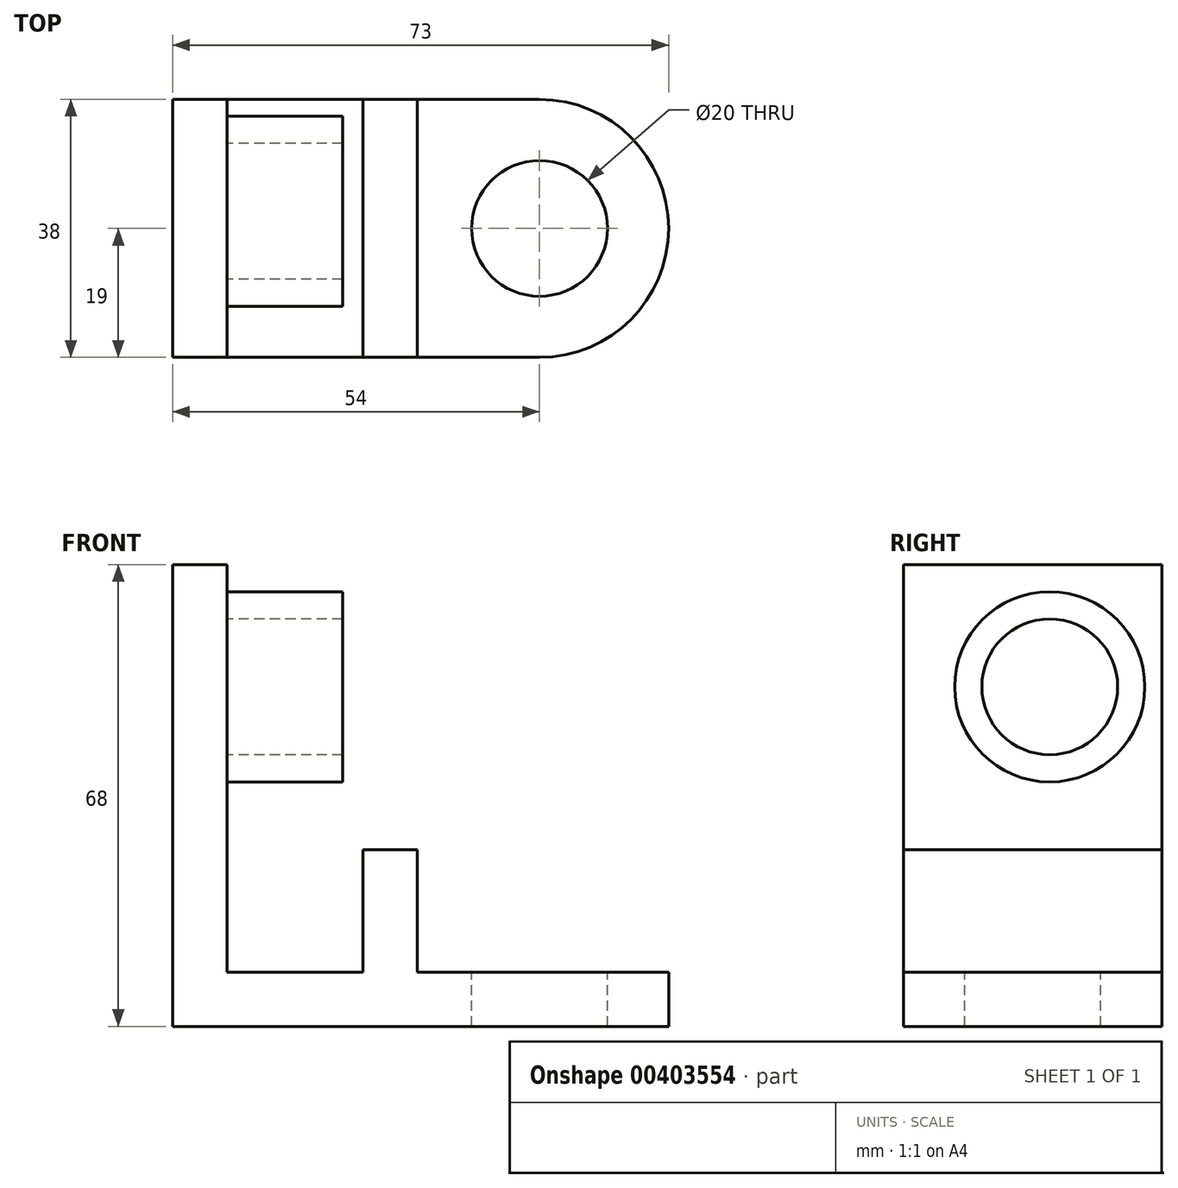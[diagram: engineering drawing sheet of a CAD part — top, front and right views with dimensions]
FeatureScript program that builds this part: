
annotation { "Feature Type Name" : "Feature", "Feature Type Description" : "" }
export const myFeature = defineFeature(function(context is Context, id is Id, definition is map)
    precondition{}
    {
        {
            var Q0;
            Q0=qCreatedBy(makeId("Front.planeOp"),FACE);
            var sketch = newSketch(context, id + "F0", { "sketchPlane" : qUnion([Q0])});
            skLineSegment(sketch, "E0", {"start": v(0, 0) * mm, "end": v(0, 68) * mm});
            skLineSegment(sketch, "E1", {"start": v(0, 68) * mm, "end": v(8, 68) * mm});
            skLineSegment(sketch, "E2", {"start": v(8, 68) * mm, "end": v(8, 8) * mm});
            skLineSegment(sketch, "E3", {"start": v(8, 8) * mm, "end": v(73, 8) * mm});
            skLineSegment(sketch, "E4", {"start": v(73, 8) * mm, "end": v(73, 0) * mm});
            skLineSegment(sketch, "E5", {"start": v(73, 0) * mm, "end": v(0, 0) * mm});
            skSolve(sketch);
        }
        {
            var Q0;
            Q0 = qSketchRegion(id + "F0", true);
            extrude(context, id + "F1", {"entities" : qUnion([Q0]), "endBound" : BoundingType.SYMMETRIC, "depth" : 38 * mm});
        }
        {
            var Q0;
            Q0=makeQuery(id+"F1.opExtrude","SWEPT_FACE",FACE,{"disambiguationData":[OSD([sQuery(id+"F0.wireOp",EDGE,"E2")])]});
            var sketch = newSketch(context, id + "F2", { "sketchPlane" : qUnion([Q0])});
            skCircle(sketch, "E6", {"center": v(2.52, 50) * mm, "radius": 14 * mm});
            skCircle(sketch, "E7", {"center": v(2.52, 50) * mm, "radius": 10 * mm});
            skSolve(sketch);
        }
        {
            var Q0;
            Q0 = qSketchRegion(id + "F2", true);
            extrude(context, id + "F3", {"entities" : qUnion([Q0]), "operationType" : NewBodyOperationType.ADD, "depth" : 17 * mm});
        }
        {
            var Q0;
            Q0=makeQuery(id+"F1.opExtrude","CAP_EDGE",EDGE,{"disambiguationData":[OSD([sQuery(id+"F0.wireOp",EDGE,"E4")])],"isStart":false});
            var Q1;
            Q1=makeQuery(id+"F1.opExtrude","CAP_EDGE",EDGE,{"disambiguationData":[OSD([sQuery(id+"F0.wireOp",EDGE,"E4")])],"isStart":true});
            fillet(context, id + "F4", {"entities" : qUnion([Q0, Q1]), "radius" : 19 * mm, "tangentPropagation" : true, "allowEdgeOverflow" : false});
        }
        {
            var Q0;
            Q0=makeQuery(id+"F1.opExtrude","SWEPT_FACE",FACE,{"disambiguationData":[OSD([sQuery(id+"F0.wireOp",EDGE,"E3")])]});
            var sketch = newSketch(context, id + "F5", { "sketchPlane" : qUnion([Q0])});
            skCircle(sketch, "E8", {"center": v(54, 0) * mm, "radius": 10 * mm});
            skSolve(sketch);
        }
        {
            var Q0;
            Q0 = qSketchRegion(id + "F5", true);
            extrude(context, id + "F6", {"entities" : qUnion([Q0]), "operationType" : NewBodyOperationType.REMOVE, "endBound" : BoundingType.THROUGH_ALL, "oppositeDirection" : true, "depth" : 25 * mm});
        }
        {
            var Q0;
            Q0=makeQuery(id+"F1.opExtrude","CAP_FACE",FACE,{"disambiguationData":[OSD([sQuery(id+"F0.wireOp",EDGE,"E0"),sQuery(id+"F0.wireOp",EDGE,"E1"),sQuery(id+"F0.wireOp",EDGE,"E2"),sQuery(id+"F0.wireOp",EDGE,"E3"),sQuery(id+"F0.wireOp",EDGE,"E4"),sQuery(id+"F0.wireOp",EDGE,"E5")])],"isStart":false});
            var sketch = newSketch(context, id + "F7", { "sketchPlane" : qUnion([Q0])});
            skLineSegment(sketch, "E9.bottom", {"start": v(36, 8) * mm, "end": v(28, 8) * mm});
            skLineSegment(sketch, "E9.top", {"start": v(36, 26) * mm, "end": v(28, 26) * mm});
            skLineSegment(sketch, "E9.left", {"start": v(36, 8) * mm, "end": v(36, 26) * mm});
            skLineSegment(sketch, "E9.right", {"start": v(28, 8) * mm, "end": v(28, 26) * mm});
            skSolve(sketch);
        }
        {
            var Q0;
            Q0 = qSketchRegion(id + "F7", true);
            var Q1;
            Q1=makeQuery(id+"F1.opExtrude","CAP_FACE",FACE,{"disambiguationData":[OSD([sQuery(id+"F0.wireOp",EDGE,"E0"),sQuery(id+"F0.wireOp",EDGE,"E1"),sQuery(id+"F0.wireOp",EDGE,"E2"),sQuery(id+"F0.wireOp",EDGE,"E3"),sQuery(id+"F0.wireOp",EDGE,"E4"),sQuery(id+"F0.wireOp",EDGE,"E5")])],"isStart":true});
            extrude(context, id + "F8", {"entities" : qUnion([Q0]), "operationType" : NewBodyOperationType.ADD, "endBound" : BoundingType.UP_TO_SURFACE, "oppositeDirection" : true, "endBoundEntityFace" : qUnion([Q1]), "depth" : 25 * mm});
        }
    });
